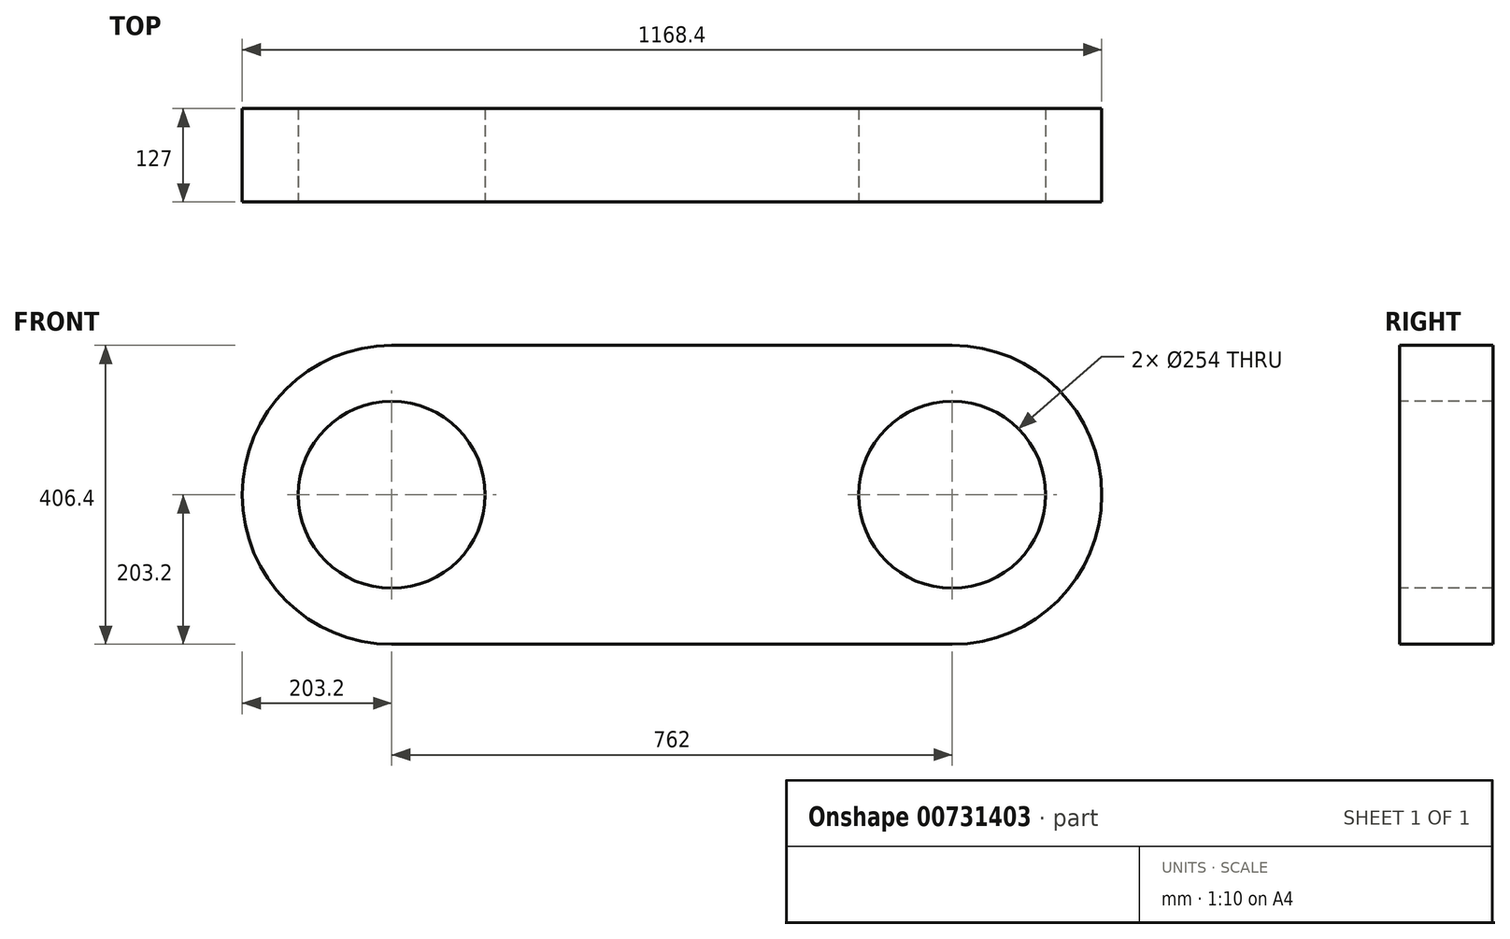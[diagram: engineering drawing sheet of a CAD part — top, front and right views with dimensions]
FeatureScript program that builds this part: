
annotation { "Feature Type Name" : "Feature", "Feature Type Description" : "" }
export const myFeature = defineFeature(function(context is Context, id is Id, definition is map)
    precondition{}
    {
        {
            var Q0;
            Q0=qCreatedBy(makeId("Front.planeOp"),FACE);
            var sketch = newSketch(context, id + "F0", { "sketchPlane" : qUnion([Q0])});
            skLineSegment(sketch, "E0.bottom", {"start": v(-381, 203.2) * mm, "end": v(381, 203.2) * mm});
            skLineSegment(sketch, "E0.top", {"start": v(-381, -203.2) * mm, "end": v(381, -203.2) * mm});
            skLineSegment(sketch, "E0.left", {"start": v(-381, 203.2) * mm, "end": v(-381, -203.2) * mm});
            skArc(sketch, "E1", {"start": v(381, -203.2) * mm, "mid": v(584.2, 0) * mm, "end": v(381, 203.2) * mm});
            skArc(sketch, "E2.MirrorCS", {"start": v(-381, -203.2) * mm, "mid": v(-584.2, 0) * mm, "end": v(-381, 203.2) * mm});
            skSolve(sketch);
        }
        {
            var Q0;
            Q0=makeQuery(id+"F0.imprint","IMPRINT",FACE,{"disambiguationData":[TD([[makeQuery(id+"F0.imprint","IMPRINT",EDGE,{"derivedFrom":sQuery(id+"F0.wireOp",EDGE,"E0.bottom")}),-1.0]])]});
            var Q1;
            Q1=makeQuery(id+"F0.imprint","IMPRINT",FACE,{"disambiguationData":[TD([[makeQuery(id+"F0.imprint","IMPRINT",EDGE,{"derivedFrom":sQuery(id+"F0.wireOp",EDGE,"E0.left")}),-1.0]])]});
            extrude(context, id + "F1", {"entities" : qUnion([Q0, Q1]), "depth" : 127 * mm, "offsetDistance" : 25.4 * mm});
        }
        {
            var Q0;
            Q0=makeQuery(id+"F1.opExtrude","CAP_FACE",FACE,{"disambiguationData":[OSD([sQuery(id+"F0.wireOp",EDGE,"E0.bottom"),sQuery(id+"F0.wireOp",EDGE,"E0.top"),sQuery(id+"F0.wireOp",EDGE,"E1"),sQuery(id+"F0.wireOp",EDGE,"E2.MirrorCS")])],"isStart":false});
            var sketch = newSketch(context, id + "F2", { "sketchPlane" : qUnion([Q0])});
            skCircle(sketch, "E3", {"center": v(381, 0) * mm, "radius": 127 * mm});
            skCircle(sketch, "E4.MirrorC", {"center": v(-381, 0) * mm, "radius": 127 * mm});
            skSolve(sketch);
        }
        {
            var Q0;
            Q0 = qSketchRegion(id + "F2", true);
            extrude(context, id + "F3", {"entities" : qUnion([Q0]), "operationType" : NewBodyOperationType.REMOVE, "oppositeDirection" : true, "depth" : 322.58 * mm, "offsetDistance" : 25.4 * mm});
        }
    });
